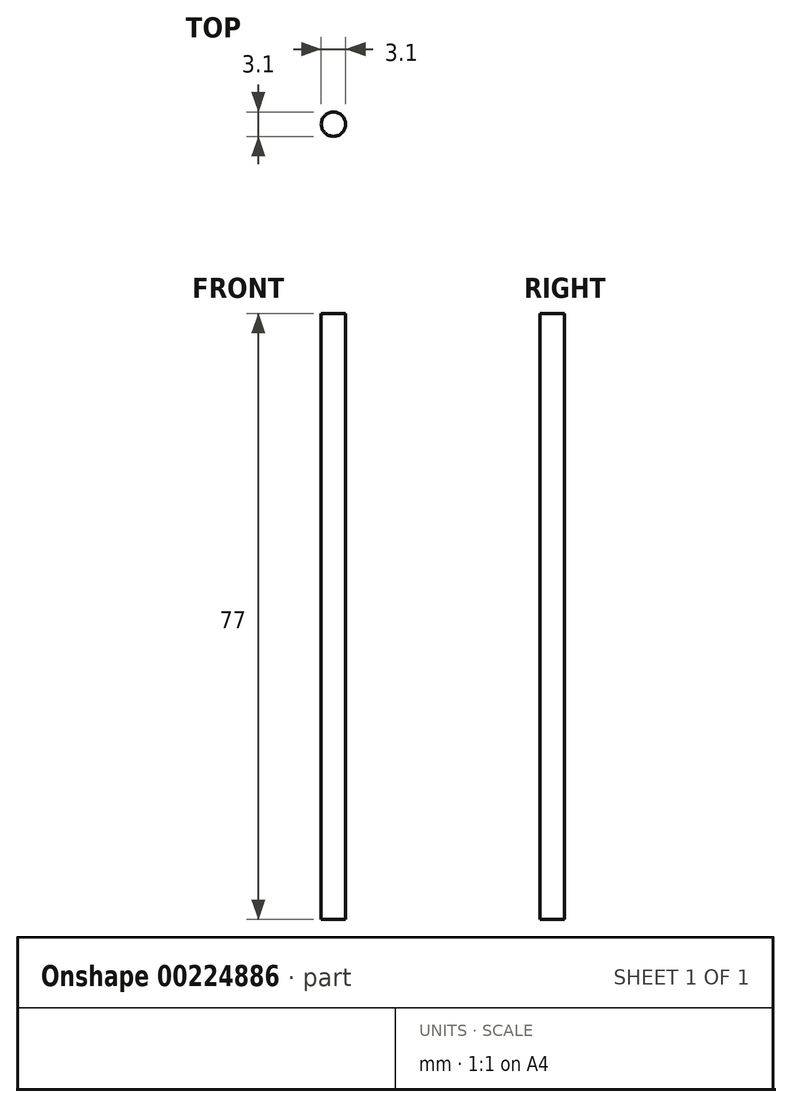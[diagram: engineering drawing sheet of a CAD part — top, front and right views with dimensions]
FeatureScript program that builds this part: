
annotation { "Feature Type Name" : "Feature", "Feature Type Description" : "" }
export const myFeature = defineFeature(function(context is Context, id is Id, definition is map)
    precondition{}
    {
        {
            var Q0;
            Q0=qCreatedBy(makeId("Top.planeOp"),FACE);
            var sketch = newSketch(context, id + "F0", { "sketchPlane" : qUnion([Q0])});
            skCircle(sketch, "E0", {"center": v(0, 0) * mm, "radius": 1.55 * mm});
            skSolve(sketch);
        }
        {
            var Q0;
            Q0=makeQuery(id+"F0.imprint","IMPRINT",FACE,{"disambiguationData":[TD([[makeQuery(id+"F0.imprint","IMPRINT",EDGE,{"derivedFrom":sQuery(id+"F0.wireOp",EDGE,"E0")}),1.0]])]});
            extrude(context, id + "F1", {"entities" : qUnion([Q0]), "endBound" : BoundingType.SYMMETRIC, "depth" : 77 * mm});
        }
    });
